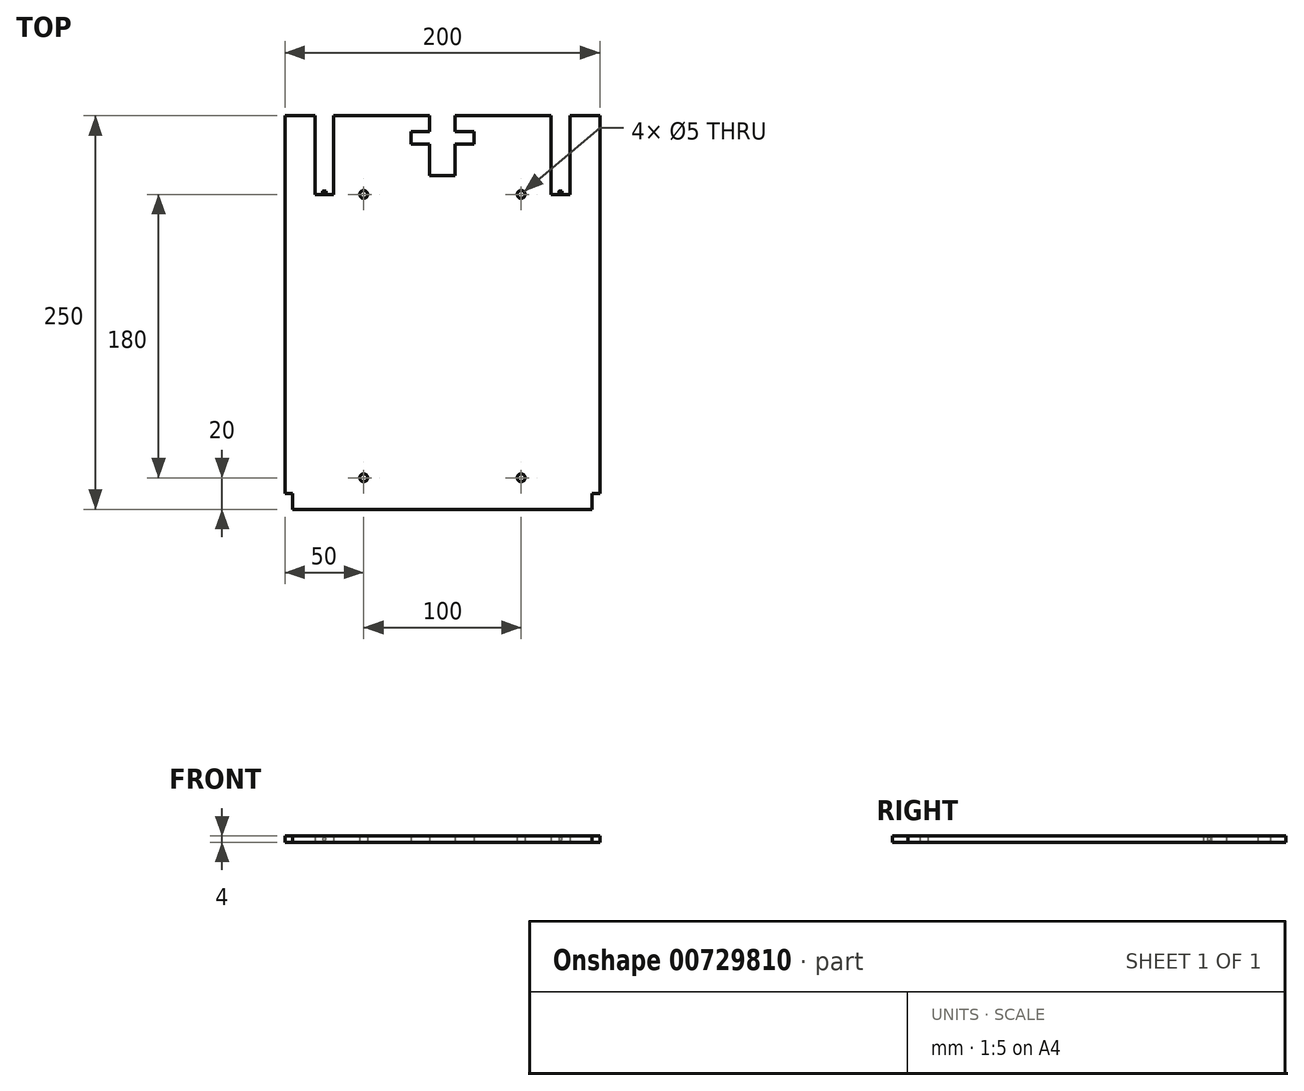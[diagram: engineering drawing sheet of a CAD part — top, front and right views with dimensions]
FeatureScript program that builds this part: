
annotation { "Feature Type Name" : "Feature", "Feature Type Description" : "" }
export const myFeature = defineFeature(function(context is Context, id is Id, definition is map)
    precondition{}
    {
        {
            var Q0;
            Q0=qCreatedBy(makeId("Top.planeOp"),FACE);
            var sketch = newSketch(context, id + "F0", { "sketchPlane" : qUnion([Q0])});
            skLineSegment(sketch, "E0.top", {"start": v(0, 50) * mm, "end": v(150, 50) * mm, "construction": true});
            skLineSegment(sketch, "E0.left", {"start": v(0, 0) * mm, "end": v(0, 50) * mm, "construction": true});
            skLineSegment(sketch, "E0.right", {"start": v(150, 0) * mm, "end": v(150, 50) * mm, "construction": true});
            skLineSegment(sketch, "E1.0", {"start": v(-6, 0) * mm, "end": v(-6, 50) * mm});
            skLineSegment(sketch, "E2.0", {"start": v(6, 0) * mm, "end": v(6, 50) * mm});
            skLineSegment(sketch, "E3.0", {"start": v(156, 0) * mm, "end": v(156, 50) * mm});
            skLineSegment(sketch, "E4.0", {"start": v(144, 0) * mm, "end": v(144, 50) * mm});
            skLineSegment(sketch, "E5", {"start": v(-6, 0) * mm, "end": v(6, 0) * mm});
            skLineSegment(sketch, "E6", {"start": v(144, 0) * mm, "end": v(156, 0) * mm});
            skLineSegment(sketch, "E7", {"start": v(156, 50) * mm, "end": v(175, 50) * mm});
            skLineSegment(sketch, "E8", {"start": v(175, 50) * mm, "end": v(175, -190) * mm});
            skLineSegment(sketch, "E9", {"start": v(170, -200) * mm, "end": v(-20, -200) * mm});
            skLineSegment(sketch, "E10", {"start": v(-25, 50) * mm, "end": v(-6, 50) * mm});
            skLineSegment(sketch, "E11", {"start": v(6, 50) * mm, "end": v(67, 50) * mm});
            skLineSegment(sketch, "E12", {"start": v(83, 50) * mm, "end": v(144, 50) * mm});
            skLineSegment(sketch, "E13", {"start": v(75, 12) * mm, "end": v(75, 50) * mm, "construction": true});
            skLineSegment(sketch, "E14.0", {"start": v(83, 12) * mm, "end": v(83, 32) * mm});
            skLineSegment(sketch, "E15.0", {"start": v(67, 12) * mm, "end": v(67, 32) * mm});
            skLineSegment(sketch, "E16", {"start": v(67, 40) * mm, "end": v(55, 40) * mm});
            skLineSegment(sketch, "E17", {"start": v(55, 40) * mm, "end": v(55, 32) * mm});
            skLineSegment(sketch, "E18", {"start": v(55, 32) * mm, "end": v(67, 32) * mm});
            skLineSegment(sketch, "E19", {"start": v(83, 32) * mm, "end": v(95, 32) * mm});
            skLineSegment(sketch, "E20", {"start": v(95, 32) * mm, "end": v(95, 40) * mm});
            skLineSegment(sketch, "E21", {"start": v(95, 40) * mm, "end": v(83, 40) * mm});
            skLineSegment(sketch, "E22", {"start": v(67, 50) * mm, "end": v(67, 40) * mm});
            skLineSegment(sketch, "E23", {"start": v(83, 50) * mm, "end": v(83, 40) * mm});
            skLineSegment(sketch, "E24", {"start": v(67, 50) * mm, "end": v(75, 50) * mm, "construction": true});
            skLineSegment(sketch, "E25", {"start": v(83, 50) * mm, "end": v(75, 50) * mm, "construction": true});
            skLineSegment(sketch, "E26", {"start": v(-25, -190) * mm, "end": v(-25, 50) * mm});
            skLineSegment(sketch, "E27", {"start": v(-20, -190) * mm, "end": v(-20, -200) * mm});
            skLineSegment(sketch, "E28", {"start": v(170, -200) * mm, "end": v(170, -190) * mm});
            skLineSegment(sketch, "E29", {"start": v(170, -190) * mm, "end": v(175, -190) * mm});
            skLineSegment(sketch, "E30", {"start": v(-25, -190) * mm, "end": v(-20, -190) * mm});
            skLineSegment(sketch, "E31", {"start": v(67, 12) * mm, "end": v(83, 12) * mm});
            skLineSegment(sketch, "E32", {"start": v(75, -200) * mm, "end": v(75, -90) * mm, "construction": true});
            skLineSegment(sketch, "E33.bottom", {"start": v(125, 0) * mm, "end": v(25, 0) * mm, "construction": true});
            skLineSegment(sketch, "E33.top", {"start": v(125, -180) * mm, "end": v(25, -180) * mm, "construction": true});
            skLineSegment(sketch, "E33.left", {"start": v(125, 0) * mm, "end": v(125, -180) * mm, "construction": true});
            skLineSegment(sketch, "E33.right", {"start": v(25, 0) * mm, "end": v(25, -180) * mm, "construction": true});
            skPoint(sketch, "E33.middle", {"position": v(75, -90) * mm});
            skCircle(sketch, "E34", {"center": v(25, 0) * mm, "radius": 2.5 * mm});
            skCircle(sketch, "E35", {"center": v(125, 0) * mm, "radius": 2.5 * mm});
            skCircle(sketch, "E36", {"center": v(25, -180) * mm, "radius": 2.5 * mm});
            skCircle(sketch, "E37", {"center": v(125, -180) * mm, "radius": 2.5 * mm});
            skSolve(sketch);
        }
        {
            var Q0;
            Q0=qSketchRegion(id+"F0",true);
            extrude(context, id + "F1", {"entities" : qUnion([Q0]), "depth" : 2 * mm, "offsetDistance" : 25 * mm, "hasSecondDirection" : true, "secondDirectionOppositeDirection" : true, "secondDirectionDepth" : 2 * mm});
        }
        {
            var Q0;
            Q0=makeQuery(id+"F1.opExtrude","SWEPT_FACE",FACE,{"disambiguationData":[OSD([sQuery(id+"F0.wireOp",EDGE,"E6")])]});
            var sketch = newSketch(context, id + "F2", { "sketchPlane" : qUnion([Q0])});
            skLineSegment(sketch, "E38", {"start": v(-144, 0) * mm, "end": v(-150, 0) * mm, "construction": true});
            skLineSegment(sketch, "E39", {"start": v(-150, 0) * mm, "end": v(-150, 2) * mm, "construction": true});
            skCircle(sketch, "E40", {"center": v(-150, 0) * mm, "radius": 1 * mm});
            skCircle(sketch, "E41", {"center": v(0, 0) * mm, "radius": 1 * mm});
            skSolve(sketch);
        }
        {
            var Q0;
            Q0=qSketchRegion(id+"F2",true);
            extrude(context, id + "F3", {"entities" : qUnion([Q0]), "operationType" : NewBodyOperationType.ADD, "depth" : 2 * mm, "offsetDistance" : 25 * mm});
        }
    });
